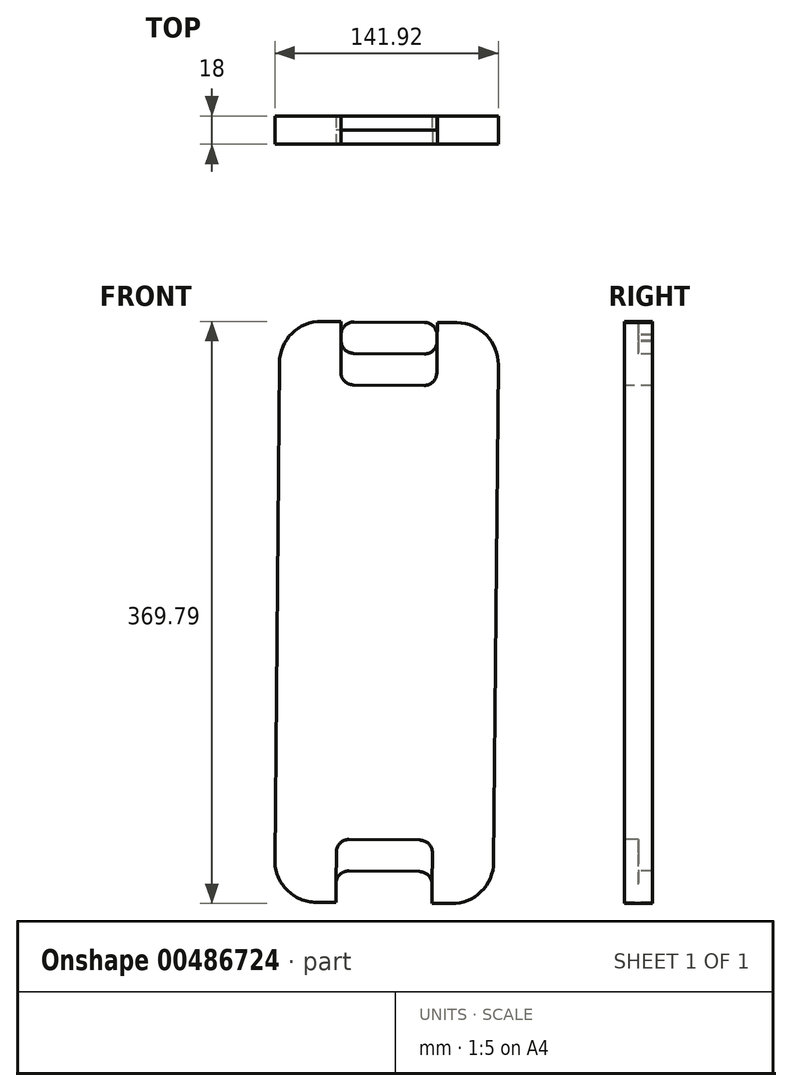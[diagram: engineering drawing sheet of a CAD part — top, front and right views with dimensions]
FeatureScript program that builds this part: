
annotation { "Feature Type Name" : "Feature", "Feature Type Description" : "" }
export const myFeature = defineFeature(function(context is Context, id is Id, definition is map)
    precondition{}
    {
        {
            var Q0;
            Q0=qCreatedBy(makeId("Front.planeOp"),FACE);
            var sketch = newSketch(context, id + "F0", { "sketchPlane" : qUnion([Q0])});
            skLineSegment(sketch, "E0", {"start": v(-90.3, -86.3) * mm, "end": v(-45.3, -86.72) * mm});
            skArc(sketch, "E1", {"start": v(-45.3, -86.72) * mm, "mid": v(-39.66, -89.11) * mm, "end": v(-37.37, -94.8) * mm});
            skLineSegment(sketch, "E2", {"start": v(-37.37, -94.8) * mm, "end": v(-37.49, -106.9) * mm});
            skLineSegment(sketch, "E3", {"start": v(-37.49, -106.9) * mm, "end": v(-24.99, -107.02) * mm});
            skArc(sketch, "E4", {"start": v(-24.99, -107.02) * mm, "mid": v(-6.18, -99.43) * mm, "end": v(1.76, -80.76) * mm});
            skLineSegment(sketch, "E5", {"start": v(1.76, -80.76) * mm, "end": v(4.68, 235.22) * mm});
            skArc(sketch, "E6", {"start": v(4.68, 235.22) * mm, "mid": v(-2.9, 254.03) * mm, "end": v(-21.57, 261.97) * mm});
            skLineSegment(sketch, "E7", {"start": v(-21.57, 261.97) * mm, "end": v(-34.07, 262.08) * mm});
            skLineSegment(sketch, "E8", {"start": v(-34.07, 262.08) * mm, "end": v(-34.18, 249.97) * mm});
            skArc(sketch, "E9", {"start": v(-34.18, 249.97) * mm, "mid": v(-36.58, 244.34) * mm, "end": v(-42.26, 242.05) * mm});
            skLineSegment(sketch, "E10", {"start": v(-42.26, 242.05) * mm, "end": v(-87.25, 242.47) * mm});
            skArc(sketch, "E11", {"start": v(-87.25, 242.47) * mm, "mid": v(-92.89, 244.86) * mm, "end": v(-95.18, 250.54) * mm});
            skLineSegment(sketch, "E12", {"start": v(-95.18, 250.54) * mm, "end": v(-95.07, 262.65) * mm});
            skLineSegment(sketch, "E13", {"start": v(-95.07, 262.65) * mm, "end": v(-107.57, 262.76) * mm});
            skArc(sketch, "E14", {"start": v(-107.57, 262.76) * mm, "mid": v(-126.38, 255.18) * mm, "end": v(-134.31, 236.51) * mm});
            skLineSegment(sketch, "E15", {"start": v(-134.31, 236.51) * mm, "end": v(-137.24, -79.48) * mm});
            skArc(sketch, "E16", {"start": v(-137.24, -79.48) * mm, "mid": v(-129.65, -98.29) * mm, "end": v(-110.98, -106.22) * mm});
            skLineSegment(sketch, "E17", {"start": v(-110.98, -106.22) * mm, "end": v(-98.48, -106.34) * mm});
            skLineSegment(sketch, "E18", {"start": v(-98.48, -106.34) * mm, "end": v(-98.37, -94.23) * mm});
            skArc(sketch, "E19", {"start": v(-98.37, -94.23) * mm, "mid": v(-95.98, -88.6) * mm, "end": v(-90.3, -86.3) * mm});
            skArc(sketch, "E20", {"start": v(-98.4, -98.23) * mm, "mid": v(-96.12, -103.9) * mm, "end": v(-90.48, -106.3) * mm});
            skLineSegment(sketch, "E21", {"start": v(-90.48, -106.3) * mm, "end": v(-45.48, -106.72) * mm});
            skArc(sketch, "E22", {"start": v(-45.48, -106.72) * mm, "mid": v(-39.8, -104.43) * mm, "end": v(-37.41, -98.8) * mm});
            skLineSegment(sketch, "E23", {"start": v(-37.41, -98.8) * mm, "end": v(-37.19, -74.8) * mm});
            skArc(sketch, "E24", {"start": v(-37.19, -74.8) * mm, "mid": v(-39.48, -69.11) * mm, "end": v(-45.11, -66.72) * mm});
            skLineSegment(sketch, "E25", {"start": v(-45.11, -66.72) * mm, "end": v(-90.11, -66.3) * mm});
            skArc(sketch, "E26", {"start": v(-90.11, -66.3) * mm, "mid": v(-95.8, -68.6) * mm, "end": v(-98.19, -74.23) * mm});
            skLineSegment(sketch, "E27", {"start": v(-98.19, -74.23) * mm, "end": v(-98.4, -98.23) * mm});
            skLineSegment(sketch, "E28", {"start": v(-87.07, 262.46) * mm, "end": v(-42.07, 262.05) * mm});
            skArc(sketch, "E29", {"start": v(-42.07, 262.05) * mm, "mid": v(-36.44, 259.65) * mm, "end": v(-34.14, 253.97) * mm});
            skLineSegment(sketch, "E30", {"start": v(-34.14, 253.97) * mm, "end": v(-34.37, 229.98) * mm});
            skArc(sketch, "E31", {"start": v(-34.37, 229.98) * mm, "mid": v(-36.76, 224.34) * mm, "end": v(-42.44, 222.05) * mm});
            skLineSegment(sketch, "E32", {"start": v(-42.44, 222.05) * mm, "end": v(-87.44, 222.47) * mm});
            skArc(sketch, "E33", {"start": v(-87.44, 222.47) * mm, "mid": v(-93.07, 224.86) * mm, "end": v(-95.36, 230.54) * mm});
            skLineSegment(sketch, "E34", {"start": v(-95.36, 230.54) * mm, "end": v(-95.14, 254.54) * mm});
            skArc(sketch, "E35", {"start": v(-95.14, 254.54) * mm, "mid": v(-92.75, 260.17) * mm, "end": v(-87.07, 262.46) * mm});
            skSolve(sketch);
        }
        {
            var Q0;
            {var subQ6=sQuery(id+"F0.wireOp",EDGE,"E2");Q0=makeQuery(id+"F0.imprint","IMPRINT",FACE,{"disambiguationData":[TD([[makeQuery(id+"F0.imprint","IMPRINT",EDGE,{"derivedFrom":subQ6}),1.0]])]});}
            var Q1;
            Q1=makeQuery(id+"F0.imprint","IMPRINT",FACE,{"disambiguationData":[TD([[makeQuery(id+"F0.imprint","IMPRINT",EDGE,{"derivedFrom":sQuery(id+"F0.wireOp",EDGE,"E0")}),1.0]])]});
            var Q2;
            {var subQ1=sQuery(id+"F0.wireOp",EDGE,"E9");Q2=makeQuery(id+"F0.imprint","IMPRINT",FACE,{"disambiguationData":[TD([[makeQuery(id+"F0.imprint","IMPRINT",EDGE,{"derivedFrom":subQ1}),1.0]])]});}
            var Q3;
            Q3=qConstructionFilter(qBodyType(qCreatedBy(id+"F0",EDGE),BodyType.WIRE),ConstructionObject.NO);
            extrude(context, id + "F1", {"entities" : qUnion([Q0, Q1, Q2]), "surfaceEntities" : qUnion([Q3]), "oppositeDirection" : true, "depth" : 18 * mm});
        }
        {
            var Q0;
            Q0=makeQuery(id+"F0.imprint","IMPRINT",FACE,{"disambiguationData":[TD([[makeQuery(id+"F0.imprint","IMPRINT",EDGE,{"derivedFrom":sQuery(id+"F0.wireOp",EDGE,"E0")}),1.0]])]});
            var Q1;
            {var subQ1=sQuery(id+"F0.wireOp",EDGE,"E9");Q1=makeQuery(id+"F0.imprint","IMPRINT",FACE,{"disambiguationData":[TD([[makeQuery(id+"F0.imprint","IMPRINT",EDGE,{"derivedFrom":subQ1}),1.0]])]});}
            extrude(context, id + "F2", {"entities" : qUnion([Q0, Q1]), "operationType" : NewBodyOperationType.REMOVE, "oppositeDirection" : true, "depth" : 9 * mm});
        }
    });
